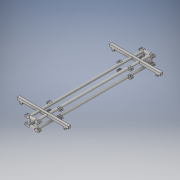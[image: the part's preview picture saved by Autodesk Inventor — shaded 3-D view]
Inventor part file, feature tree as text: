
AUTODESK INVENTOR PART (.ipt)
format: ipt  version: 2016 (Build 200138000, 138)  size: 501,248 bytes
history: native  units: in
note: dims shown in document units (in); Inventor stores cm internally (conversion verified against a paired STEP export)
features: sketch x12, extrude x11, plane x4, projected_geometry x3, fillet x2, mirror x2
ambient origin geometry x8: Origin, YZ Plane, XZ Plane, XY Plane, X Axis, Y Axis, Z Axis, Center Point
bodies: Solid1 (feature_tree)
feature tree (34):
  extrude  "Extrusion1"  Depth=6.0in
  sketch  "Sketch2"  dims[d6=2.0in d7=96.0in d8=0.0in]
  plane  "Work Plane1"
  extrude  "Extrusion2"  Depth=96.0in TaperAngle=0.0deg
  plane  "Work Plane2"
  extrude  "Extrusion3"  Depth=2.0in
  plane  "Work Plane3"
  extrude  "Extrusion4"  TaperAngle=90.0deg  [1 undecoded]
  extrude  "Extrusion5"  Depth=6.0in TaperAngle=0.0deg
  extrude  "Extrusion6"  Depth=2.0in
  fillet  "Fillet1"  Radius=2.0in
  extrude  "Extrusion7"  Depth=2.0in
  extrude  "Extrusion8"  Depth=2.0in
  mirror  "Mirror1"
  plane  "Work Plane4"
  mirror  "Mirror2"
  extrude  "Extrusion9"  Depth=18.0in
  extrude  "Extrusion10"  Depth=2.0in
  fillet  "Fillet2"  Radius=2.0in
  extrude  "Extrusion11"  Depth=2.0in TaperAngle=0.0deg
  sketch  "Sketch1"  dims[d0=6.0in d1=6.0in]
  projected_geometry  "Projected Loop1"
  projected_geometry  "Projected Loop2"
  projected_geometry  "Projected Loop3"
  sketch  "Sketch3"  dims[d9=90.0deg d10=2.0in]
  sketch  "Sketch4"  dims[d11=6.0in d12=0.0in d13=90.0deg]
  sketch  "Sketch7"  dims[d14=2.0in d18=6.0in d19=0.0in]
  sketch  "Sketch9"  dims[d22=3.0in d23=2.0in d24=2.0in]
  sketch  "Sketch10"  dims[d25=42.0in d26=0.0in d27=2.0in]
  sketch  "Sketch11"  dims[d28=2.0in d29=2.0in]
  sketch  "Sketch12"  dims[d30=2.0in d31=18.0in]
  sketch  "Sketch13"  dims[d32=2.0in d33=2.0in d34=2.0in]
  sketch  "Sketch14"  dims[d35=2.0in d36=3.0in d37=0.0in]
  sketch  "Sketch15"  dims[d38=2.0in d39=0.0in d40=1.0in d41=3.0in d42=0.0in d43=3.0in d44=0.0in d49=2.0in d50=2.0in d51=2.0in d52=0.0in d53=1.5in d54=0.0in d55=1.0in d56=100.0in d57=0.0in]
note: 1 required parameter value undecoded (feature->parameter linkage not recoverable at this tier; creation-order binding heuristic only, values carry confidence <= 0.55)
